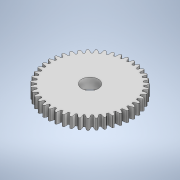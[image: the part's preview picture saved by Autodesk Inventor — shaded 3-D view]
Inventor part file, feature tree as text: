
AUTODESK INVENTOR PART (.ipt)
format: ipt  version: 2020 (Build 240168000, 168)  size: 522,240 bytes
history: native  units: mm
features: extrude x2, sketch x2, fillet x1, pattern_circular x1
ambient origin geometry x8: Origin, YZ Plane, XZ Plane, XY Plane, X Axis, Y Axis, Z Axis, Center Point
bodies: Solid1 (feature_tree)
feature tree (6):
  extrude  "Extrusion1"  Depth=7.0mm TaperAngle=360.0deg
  fillet  "Fillet2"  Radius=53.15mm
  pattern_circular  "Circular Pattern2"  [2 undecoded]
  extrude  "Extrusion3"  Depth=0.4mm
  sketch  "Sketch1"  dims[d4=7.0mm d5=0.0mm d18=430.0mm d19=360.0deg d23=53.15mm]
  sketch  "Sketch3"  dims[d25=1.545058mm d26=1.236047mm d27=3.490659mm d28=49.944663mm d29=3.490659mm d30=0.309012mm d31=0.618023mm d32=0.970791mm d33=0.4mm d34=11.0mm d35=3.0mm d36=0.0mm]
note: 2 required parameter values undecoded (feature->parameter linkage not recoverable at this tier; creation-order binding heuristic only, values carry confidence <= 0.55)
